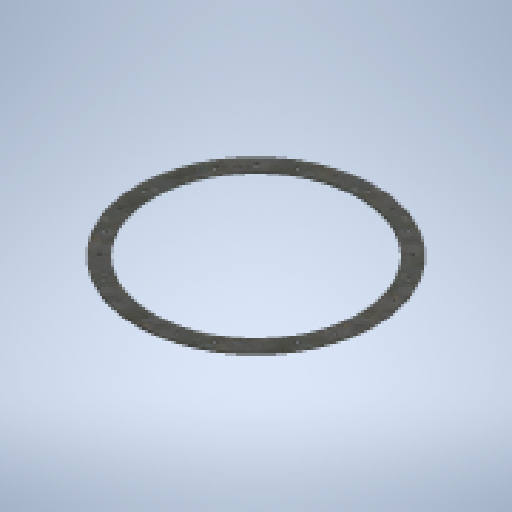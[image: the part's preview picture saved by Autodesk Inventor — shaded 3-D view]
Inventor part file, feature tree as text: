
AUTODESK INVENTOR PART (.ipt)
format: ipt  version: 2023 (Build 270158000, 158)  size: 199,168 bytes
history: native  units: mm
features: sketch x1, extrude x1, hole x1, pattern_circular x1
ambient origin geometry x8: Origin, YZ Plane, XZ Plane, XY Plane, X Axis, Y Axis, Z Axis, Center Point
bodies: Solid1 (feature_tree)
feature tree (4):
  sketch  "Sketch1"  dims[d0=840.0mm d1=720.0mm d2=14.2875mm d3=780.0mm d4=8.0mm d5=0.0mm d6=14.2875mm d7=6.0mm d8=4.0mm d9=2.0mm d10=90.0deg d11=8.0mm d12=20.594885mm d13=240.0mm d14=360.0deg]
  extrude  "Extrusion1"  Depth=8.0mm
  hole  "Hole1"  [1 undecoded]
  pattern_circular  "Circular Pattern1"  Count=78  [1 undecoded]
note: 2 required parameter values undecoded (feature->parameter linkage not recoverable at this tier; creation-order binding heuristic only, values carry confidence <= 0.55)
